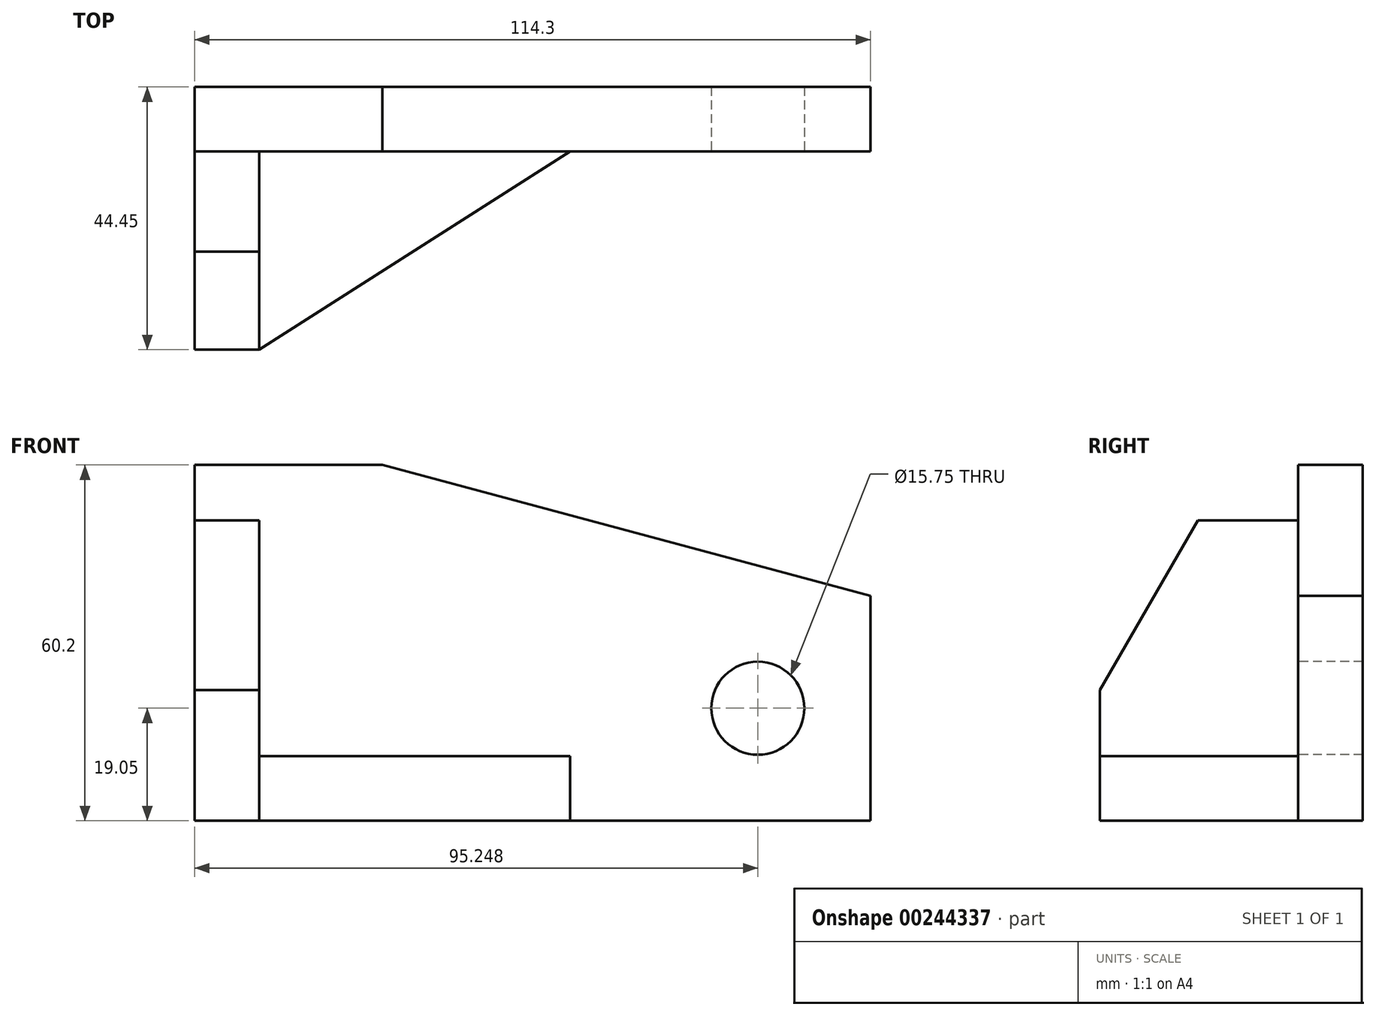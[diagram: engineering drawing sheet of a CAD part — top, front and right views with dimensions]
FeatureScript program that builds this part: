
annotation { "Feature Type Name" : "Feature", "Feature Type Description" : "" }
export const myFeature = defineFeature(function(context is Context, id is Id, definition is map)
    precondition{}
    {
        {
            var Q0;
            Q0=qCreatedBy(makeId("Top.planeOp"),FACE);
            var sketch = newSketch(context, id + "F0", { "sketchPlane" : qUnion([Q0])});
            skLineSegment(sketch, "E0.bottom", {"start": v(-32.5, 24.16) * mm, "end": v(81.8, 24.16) * mm});
            skLineSegment(sketch, "E0.top", {"start": v(-32.5, -20.29) * mm, "end": v(81.8, -20.29) * mm});
            skLineSegment(sketch, "E0.left", {"start": v(-32.5, 24.16) * mm, "end": v(-32.5, -20.29) * mm});
            skLineSegment(sketch, "E0.right", {"start": v(81.8, 24.16) * mm, "end": v(81.8, -20.29) * mm});
            skLineSegment(sketch, "E1", {"start": v(-32.5, 13.24) * mm, "end": v(81.8, 13.24) * mm});
            skLineSegment(sketch, "E2", {"start": v(-0.75, 24.16) * mm, "end": v(-0.75, 13.24) * mm});
            skLineSegment(sketch, "E3", {"start": v(-21.58, 13.24) * mm, "end": v(-21.58, -20.29) * mm});
            skLineSegment(sketch, "E4", {"start": v(-21.58, -20.29) * mm, "end": v(31, 13.24) * mm});
            skSolve(sketch);
        }
        {
            var Q0;
            {var subQ0=sQuery(id+"F0.wireOp",EDGE,"E2");Q0=makeQuery(id+"F0.imprint","IMPRINT",FACE,{"disambiguationData":[TD([[makeQuery(id+"F0.imprint","IMPRINT",EDGE,{"derivedFrom":subQ0}),-1.0]])]});}
            var Q1;
            {var subQ3=sQuery(id+"F0.wireOp",EDGE,"E2");Q1=makeQuery(id+"F0.imprint","IMPRINT",FACE,{"disambiguationData":[TD([[makeQuery(id+"F0.imprint","IMPRINT",EDGE,{"derivedFrom":subQ3}),1.0]])]});}
            extrude(context, id + "F1", {"entities" : qUnion([Q0, Q1]), "depth" : 60.2 * mm});
        }
        {
            var Q0;
            Q0=makeQuery(id+"F1.opExtrude","SWEPT_FACE",FACE,{"disambiguationData":[OSD([sQuery(id+"F0.wireOp",EDGE,"E1")])]});
            var sketch = newSketch(context, id + "F2", { "sketchPlane" : qUnion([Q0])});
            skLineSegment(sketch, "E5", {"start": v(-0.75, 60.2) * mm, "end": v(-0.75, 0) * mm});
            skLineSegment(sketch, "E6", {"start": v(-0.75, 60.2) * mm, "end": v(81.8, 38.08) * mm});
            skLineSegment(sketch, "E7", {"start": v(-0.75, 60.2) * mm, "end": v(81.8, 60.2) * mm});
            skLineSegment(sketch, "E8", {"start": v(81.8, 60.2) * mm, "end": v(81.8, 38.08) * mm});
            skPoint(sketch, "E9", {"position": v(62.75, 19.05) * mm});
            skCircle(sketch, "E10", {"center": v(62.75, 19.05) * mm, "radius": 7.87 * mm});
            skSolve(sketch);
        }
        {
            var Q0;
            Q0=makeQuery(id+"F2.imprint","IMPRINT",FACE,{"disambiguationData":[TD([[makeQuery(id+"F2.imprint","IMPRINT",EDGE,{"derivedFrom":sQuery(id+"F2.wireOp",EDGE,"E6")}),1.0]])]});
            extrude(context, id + "F3", {"entities" : qUnion([Q0]), "operationType" : NewBodyOperationType.REMOVE, "endBound" : BoundingType.THROUGH_ALL, "oppositeDirection" : true, "depth" : 25.4 * mm});
        }
        {
            var Q0;
            {var subQ3=sQuery(id+"F0.wireOp",EDGE,"E3");Q0=makeQuery(id+"F0.imprint","IMPRINT",FACE,{"disambiguationData":[TD([[makeQuery(id+"F0.imprint","IMPRINT",EDGE,{"derivedFrom":subQ3}),-1.0]])]});}
            extrude(context, id + "F4", {"entities" : qUnion([Q0]), "operationType" : NewBodyOperationType.ADD, "depth" : 50.8 * mm});
        }
        {
            var Q0;
            Q0=makeQuery(id+"F4.opExtrude","SWEPT_FACE",FACE,{"disambiguationData":[OSD([sQuery(id+"F0.wireOp",EDGE,"E3")])]});
            var sketch = newSketch(context, id + "F5", { "sketchPlane" : qUnion([Q0])});
            skLineSegment(sketch, "E11", {"start": v(-20.29, 22.1) * mm, "end": v(13.24, 22.1) * mm});
            skLineSegment(sketch, "E12", {"start": v(-20.29, 22.1) * mm, "end": v(-3.72, 50.8) * mm});
            skSolve(sketch);
        }
        {
            var Q0;
            {var subQ0=sQuery(id+"F5.wireOp",EDGE,"E12");Q0=makeQuery(id+"F5.imprint","IMPRINT",FACE,{"disambiguationData":[TD([[makeQuery(id+"F5.imprint","IMPRINT",EDGE,{"derivedFrom":subQ0}),1.0]])]});}
            extrude(context, id + "F6", {"entities" : qUnion([Q0]), "operationType" : NewBodyOperationType.REMOVE, "endBound" : BoundingType.THROUGH_ALL, "oppositeDirection" : true, "depth" : 25.4 * mm});
        }
        {
            var Q0;
            {var subQ2=sQuery(id+"F0.wireOp",EDGE,"E3");Q0=makeQuery(id+"F0.imprint","IMPRINT",FACE,{"disambiguationData":[TD([[makeQuery(id+"F0.imprint","IMPRINT",EDGE,{"derivedFrom":subQ2}),1.0]])]});}
            extrude(context, id + "F7", {"entities" : qUnion([Q0]), "operationType" : NewBodyOperationType.ADD, "depth" : 10.92 * mm});
        }
        {
            var Q0;
            Q0=makeQuery(id+"F2.imprint","IMPRINT",FACE,{"disambiguationData":[TD([[makeQuery(id+"F2.imprint","IMPRINT",EDGE,{"derivedFrom":sQuery(id+"F2.wireOp",EDGE,"E10")}),1.0]])]});
            extrude(context, id + "F8", {"entities" : qUnion([Q0]), "operationType" : NewBodyOperationType.REMOVE, "oppositeDirection" : true, "depth" : 25.4 * mm});
        }
    });
